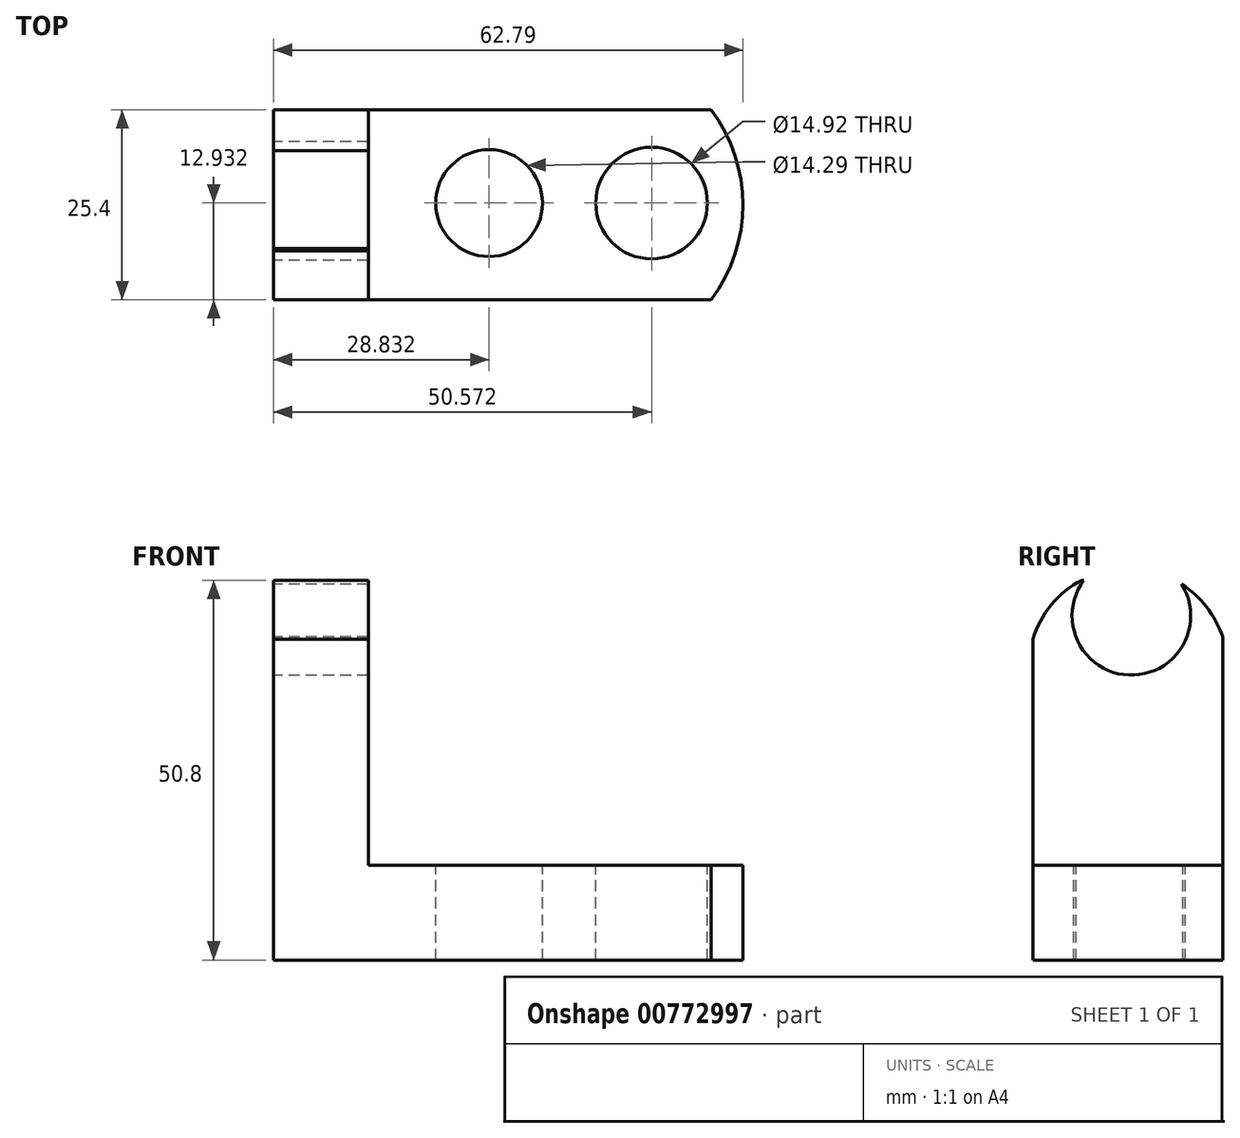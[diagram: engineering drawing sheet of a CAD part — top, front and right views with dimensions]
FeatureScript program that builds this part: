
annotation { "Feature Type Name" : "Feature", "Feature Type Description" : "" }
export const myFeature = defineFeature(function(context is Context, id is Id, definition is map)
    precondition{}
    {
        {
            var Q0;
            Q0=qCreatedBy(makeId("Front.planeOp"),FACE);
            var sketch = newSketch(context, id + "F0", { "sketchPlane" : qUnion([Q0])});
            skLineSegment(sketch, "E0", {"start": v(0, 0) * mm, "end": v(63.5, 0) * mm});
            skLineSegment(sketch, "E1", {"start": v(63.5, 0) * mm, "end": v(63.5, 50.8) * mm});
            skLineSegment(sketch, "E2", {"start": v(63.5, 50.8) * mm, "end": v(0, 50.8) * mm});
            skLineSegment(sketch, "E3", {"start": v(0, 50.8) * mm, "end": v(0, 0) * mm});
            skSolve(sketch);
        }
        {
            var Q0;
            Q0 = qSketchRegion(id + "F0", true);
            extrude(context, id + "F1", {"entities" : qUnion([Q0]), "depth" : 25.4 * mm, "offsetDistance" : 25.4 * mm});
        }
        {
            var Q0;
            Q0=makeQuery(id+"F1.opExtrude","CAP_FACE",FACE,{"disambiguationData":[OSD([sQuery(id+"F0.wireOp",EDGE,"E0"),sQuery(id+"F0.wireOp",EDGE,"E1"),sQuery(id+"F0.wireOp",EDGE,"E2"),sQuery(id+"F0.wireOp",EDGE,"E3")])],"isStart":false});
            var sketch = newSketch(context, id + "F2", { "sketchPlane" : qUnion([Q0])});
            skLineSegment(sketch, "E4", {"start": v(12.7, 50.8) * mm, "end": v(12.7, 12.7) * mm});
            skLineSegment(sketch, "E5", {"start": v(12.7, 12.7) * mm, "end": v(63.5, 12.7) * mm});
            skSolve(sketch);
        }
        {
            var Q0;
            Q0 = qSketchRegion(id + "F2", true);
            var Q1;
            {var subQ0=sQuery(id+"F2.wireOp",EDGE,"E4");Q1=makeQuery(id+"F2.imprint","IMPRINT",FACE,{"disambiguationData":[TD([[makeQuery(id+"F2.imprint","IMPRINT",EDGE,{"derivedFrom":subQ0}),1.0]])]});}
            extrude(context, id + "F3", {"entities" : qUnion([Q0, Q1]), "operationType" : NewBodyOperationType.REMOVE, "oppositeDirection" : true, "depth" : 25.4 * mm, "offsetDistance" : 25.4 * mm});
        }
        {
            var Q0;
            Q0=makeQuery(id+"F1.opExtrude","SWEPT_FACE",FACE,{"disambiguationData":[OSD([sQuery(id+"F0.wireOp",EDGE,"E3")])]});
            var sketch = newSketch(context, id + "F4", { "sketchPlane" : qUnion([Q0])});
            skArc(sketch, "E6", {"start": v(5.86, 50.8) * mm, "mid": v(12.2, 38.1) * mm, "end": v(18.56, 50.8) * mm});
            skSolve(sketch);
        }
        {
            var Q0;
            Q0 = qSketchRegion(id + "F4", true);
            var Q1;
            {var subQ0=sQuery(id+"F4.wireOp",EDGE,"E6");Q1=makeQuery(id+"F4.imprint","IMPRINT",FACE,{"disambiguationData":[TD([[makeQuery(id+"F4.imprint","IMPRINT",EDGE,{"derivedFrom":subQ0}),1.0]])]});}
            extrude(context, id + "F5", {"entities" : qUnion([Q0, Q1]), "operationType" : NewBodyOperationType.REMOVE, "oppositeDirection" : true, "depth" : 25.4 * mm, "offsetDistance" : 25.4 * mm});
        }
        {
            var Q0;
            Q0=makeQuery(id+"F1.opExtrude","SWEPT_FACE",FACE,{"disambiguationData":[OSD([sQuery(id+"F0.wireOp",EDGE,"E3")])]});
            var sketch = newSketch(context, id + "F6", { "sketchPlane" : qUnion([Q0])});
            skArc(sketch, "E7", {"start": v(25.4, 42.9) * mm, "mid": v(12.81, 52.33) * mm, "end": v(0, 43.22) * mm});
            skSolve(sketch);
        }
        {
            var Q0;
            Q0 = qSketchRegion(id + "F6", true);
            var Q1;
            {var subQ0=sQuery(id+"F6.wireOp",EDGE,"E7");var subQ1=sQuery(id+"F0.wireOp",EDGE,"E3");var subQ2=makeQuery(id+"F1.opExtrude","CAP_EDGE",EDGE,{"disambiguationData":[OSD([subQ1])],"isStart":true});var subQ3=makeQuery(id+"F6.imprint","INTERSECT",VERTEX,{"derivedFrom":[subQ2,subQ0]});Q1=makeQuery(id+"F6.imprint","IMPRINT",FACE,{"disambiguationData":[TD([[makeQuery(id+"F6.imprint","IMPRINT",EDGE,{"disambiguationData":[TD([[subQ3,1.0]])],"derivedFrom":subQ0}),-1.0]])]});}
            var Q2;
            {var subQ0=sQuery(id+"F6.wireOp",EDGE,"E7");var subQ1=sQuery(id+"F0.wireOp",EDGE,"E3");var subQ2=makeQuery(id+"F1.opExtrude","CAP_EDGE",EDGE,{"disambiguationData":[OSD([subQ1])],"isStart":false});var subQ3=makeQuery(id+"F6.imprint","INTERSECT",VERTEX,{"derivedFrom":[subQ2,subQ0]});Q2=makeQuery(id+"F6.imprint","IMPRINT",FACE,{"disambiguationData":[TD([[makeQuery(id+"F6.imprint","IMPRINT",EDGE,{"disambiguationData":[TD([[subQ3,-1.0]])],"derivedFrom":subQ0}),-1.0]])]});}
            extrude(context, id + "F7", {"entities" : qUnion([Q0, Q1, Q2]), "operationType" : NewBodyOperationType.REMOVE, "oppositeDirection" : true, "depth" : 25.4 * mm, "offsetDistance" : 25.4 * mm});
        }
        {
            var Q0;
            Q0=makeQuery(id+"F3.boolean.opBoolean","COPY",FACE,{"derivedFrom":makeQuery(id+"F3.opExtrude","SWEPT_FACE",FACE,{"disambiguationData":[OSD([sQuery(id+"F2.wireOp",EDGE,"E5")])]})});
            var sketch = newSketch(context, id + "F8", { "sketchPlane" : qUnion([Q0])});
            skCircle(sketch, "E8", {"center": v(28.83, -12.47) * mm, "radius": 7.14 * mm});
            skCircle(sketch, "E9", {"center": v(50.57, -12.47) * mm, "radius": 7.46 * mm});
            skSolve(sketch);
        }
        {
            var Q0;
            Q0=makeQuery(id+"F8.imprint","IMPRINT",FACE,{"disambiguationData":[TD([[makeQuery(id+"F8.imprint","IMPRINT",EDGE,{"derivedFrom":sQuery(id+"F8.wireOp",EDGE,"E8")}),1.0]])]});
            var Q1;
            Q1=makeQuery(id+"F8.imprint","IMPRINT",FACE,{"disambiguationData":[TD([[makeQuery(id+"F8.imprint","IMPRINT",EDGE,{"derivedFrom":sQuery(id+"F8.wireOp",EDGE,"E9")}),1.0]])]});
            extrude(context, id + "F9", {"entities" : qUnion([Q0, Q1]), "operationType" : NewBodyOperationType.REMOVE, "oppositeDirection" : true, "depth" : 25.4 * mm, "offsetDistance" : 25.4 * mm});
        }
        {
            var Q0;
            Q0=makeQuery(id+"F3.boolean.opBoolean","COPY",FACE,{"derivedFrom":makeQuery(id+"F3.opExtrude","SWEPT_FACE",FACE,{"disambiguationData":[OSD([sQuery(id+"F2.wireOp",EDGE,"E5")])]})});
            var sketch = newSketch(context, id + "F10", { "sketchPlane" : qUnion([Q0])});
            skArc(sketch, "E10", {"start": v(54.92, -25.4) * mm, "mid": v(63.85, -12.7) * mm, "end": v(54.92, 0) * mm});
            skSolve(sketch);
        }
        {
            var Q0;
            Q0 = qSketchRegion(id + "F10", true);
            var Q1;
            {var subQ0=sQuery(id+"F10.wireOp",EDGE,"E10");var subQ1=sQuery(id+"F2.wireOp",EDGE,"E5");var subQ2=makeQuery(id+"F3.boolean.opBoolean","COPY",EDGE,{"derivedFrom":makeQuery(id+"F3.opExtrude","CAP_EDGE",EDGE,{"disambiguationData":[OSD([subQ1])],"isStart":true})});var subQ3=makeQuery(id+"F10.imprint","INTERSECT",VERTEX,{"derivedFrom":[subQ2,subQ0]});Q1=makeQuery(id+"F10.imprint","IMPRINT",FACE,{"disambiguationData":[TD([[makeQuery(id+"F10.imprint","IMPRINT",EDGE,{"disambiguationData":[TD([[subQ3,-1.0]])],"derivedFrom":subQ0}),-1.0]])]});}
            var Q2;
            {var subQ0=sQuery(id+"F10.wireOp",EDGE,"E10");var subQ1=sQuery(id+"F2.wireOp",EDGE,"E5");var subQ2=makeQuery(id+"F3.boolean.opBoolean","COPY",EDGE,{"derivedFrom":makeQuery(id+"F3.opExtrude","CAP_EDGE",EDGE,{"disambiguationData":[OSD([subQ1])],"isStart":false})});var subQ3=makeQuery(id+"F10.imprint","INTERSECT",VERTEX,{"derivedFrom":[subQ2,subQ0]});Q2=makeQuery(id+"F10.imprint","IMPRINT",FACE,{"disambiguationData":[TD([[makeQuery(id+"F10.imprint","IMPRINT",EDGE,{"disambiguationData":[TD([[subQ3,1.0]])],"derivedFrom":subQ0}),-1.0]])]});}
            extrude(context, id + "F11", {"entities" : qUnion([Q0, Q1, Q2]), "operationType" : NewBodyOperationType.ADD, "depth" : 25.4 * mm, "offsetDistance" : 25.4 * mm});
        }
        {
            var Q0;
            {var subQ0=sQuery(id+"F2.wireOp",EDGE,"E5");var subQ1=makeQuery(id+"F3.boolean.opBoolean","COPY",EDGE,{"derivedFrom":makeQuery(id+"F3.opExtrude","CAP_EDGE",EDGE,{"disambiguationData":[OSD([subQ0])],"isStart":false})});var subQ2=sQuery(id+"F0.wireOp",EDGE,"E1");var subQ3=makeQuery(id+"F3.boolean.opBoolean","COPY",EDGE,{"derivedFrom":makeQuery(id+"F3.opExtrude","SWEPT_EDGE",EDGE,{"disambiguationData":[OSD([subQ2,subQ0])]})});var subQ4=makeQuery(id+"F10.imprint","INTERSECT",VERTEX,{"derivedFrom":[subQ3,subQ1]});var subQ5=sQuery(id+"F10.wireOp",EDGE,"E10");var subQ6=makeQuery(id+"F10.imprint","INTERSECT",VERTEX,{"derivedFrom":[subQ1,subQ5]});Q0=makeQuery(id+"F11.opExtrude","CAP_FACE",FACE,{"disambiguationData":[OSD([subQ2,subQ0,subQ5]),TDD([makeQuery(id+"F10.imprint","IMPRINT",EDGE,{"disambiguationData":[TD([[subQ6,1.0]])],"derivedFrom":subQ5}),makeQuery(id+"F10.imprint","IMPRINT",EDGE,{"disambiguationData":[TD([[subQ4,-1.0]])],"derivedFrom":subQ3}),makeQuery(id+"F10.imprint","IMPRINT",EDGE,{"disambiguationData":[TD([[subQ6,-1.0]])],"derivedFrom":subQ1})])],"isStart":false});}
            var Q1;
            {var subQ0=sQuery(id+"F2.wireOp",EDGE,"E5");var subQ1=makeQuery(id+"F3.boolean.opBoolean","COPY",EDGE,{"derivedFrom":makeQuery(id+"F3.opExtrude","CAP_EDGE",EDGE,{"disambiguationData":[OSD([subQ0])],"isStart":true})});var subQ2=sQuery(id+"F0.wireOp",EDGE,"E1");var subQ3=makeQuery(id+"F3.boolean.opBoolean","COPY",EDGE,{"derivedFrom":makeQuery(id+"F3.opExtrude","SWEPT_EDGE",EDGE,{"disambiguationData":[OSD([subQ2,subQ0])]})});var subQ4=makeQuery(id+"F10.imprint","INTERSECT",VERTEX,{"derivedFrom":[subQ3,subQ1]});var subQ5=sQuery(id+"F10.wireOp",EDGE,"E10");var subQ6=makeQuery(id+"F10.imprint","INTERSECT",VERTEX,{"derivedFrom":[subQ1,subQ5]});Q1=makeQuery(id+"F11.opExtrude","CAP_FACE",FACE,{"disambiguationData":[OSD([subQ2,subQ0,subQ5]),TDD([makeQuery(id+"F10.imprint","IMPRINT",EDGE,{"disambiguationData":[TD([[subQ6,-1.0]])],"derivedFrom":subQ5}),makeQuery(id+"F10.imprint","IMPRINT",EDGE,{"disambiguationData":[TD([[subQ4,1.0]])],"derivedFrom":subQ3}),makeQuery(id+"F10.imprint","IMPRINT",EDGE,{"disambiguationData":[TD([[subQ6,-1.0]])],"derivedFrom":subQ1})])],"isStart":false});}
            extrude(context, id + "F12", {"entities" : qUnion([Q0, Q1]), "operationType" : NewBodyOperationType.REMOVE, "oppositeDirection" : true, "depth" : 25.4 * mm, "offsetDistance" : 25.4 * mm});
        }
        {
            var Q0;
            {var subQ0=sQuery(id+"F2.wireOp",EDGE,"E5");var subQ1=makeQuery(id+"F3.boolean.opBoolean","COPY",EDGE,{"derivedFrom":makeQuery(id+"F3.opExtrude","CAP_EDGE",EDGE,{"disambiguationData":[OSD([subQ0])],"isStart":false})});var subQ2=sQuery(id+"F0.wireOp",EDGE,"E1");var subQ3=makeQuery(id+"F3.boolean.opBoolean","COPY",EDGE,{"derivedFrom":makeQuery(id+"F3.opExtrude","SWEPT_EDGE",EDGE,{"disambiguationData":[OSD([subQ2,subQ0])]})});var subQ4=makeQuery(id+"F10.imprint","INTERSECT",VERTEX,{"derivedFrom":[subQ3,subQ1]});var subQ5=sQuery(id+"F10.wireOp",EDGE,"E10");var subQ6=makeQuery(id+"F10.imprint","INTERSECT",VERTEX,{"derivedFrom":[subQ1,subQ5]});var subQ8=makeQuery(id+"F3.boolean.opBoolean","COPY",EDGE,{"derivedFrom":makeQuery(id+"F3.opExtrude","CAP_EDGE",EDGE,{"disambiguationData":[OSD([subQ0])],"isStart":true})});var subQ9=makeQuery(id+"F10.imprint","INTERSECT",VERTEX,{"derivedFrom":[subQ3,subQ8]});var subQ10=makeQuery(id+"F10.imprint","INTERSECT",VERTEX,{"derivedFrom":[subQ8,subQ5]});Q0=makeQuery(id+"F12.boolean.opBoolean","MERGE",FACE,{"derivedFrom":[makeQuery(id+"F3.boolean.opBoolean","COPY",FACE,{"derivedFrom":makeQuery(id+"F3.opExtrude","SWEPT_FACE",FACE,{"disambiguationData":[OSD([subQ0])]})}),makeQuery(id+"F12.opExtrude","CAP_FACE",FACE,{"disambiguationData":[OSD([subQ2,subQ0,subQ5]),TDD([makeQuery(id+"F11.opExtrude","CAP_FACE",FACE,{"disambiguationData":[OSD([subQ2,subQ0,subQ5]),TDD([makeQuery(id+"F10.imprint","IMPRINT",EDGE,{"disambiguationData":[TD([[subQ10,-1.0]])],"derivedFrom":subQ5}),makeQuery(id+"F10.imprint","IMPRINT",EDGE,{"disambiguationData":[TD([[subQ9,1.0]])],"derivedFrom":subQ3}),makeQuery(id+"F10.imprint","IMPRINT",EDGE,{"disambiguationData":[TD([[subQ10,-1.0]])],"derivedFrom":subQ8})])],"isStart":false})])],"isStart":false}),makeQuery(id+"F12.opExtrude","CAP_FACE",FACE,{"disambiguationData":[OSD([subQ2,subQ0,subQ5]),TDD([makeQuery(id+"F11.opExtrude","CAP_FACE",FACE,{"disambiguationData":[OSD([subQ2,subQ0,subQ5]),TDD([makeQuery(id+"F10.imprint","IMPRINT",EDGE,{"disambiguationData":[TD([[subQ6,1.0]])],"derivedFrom":subQ5}),makeQuery(id+"F10.imprint","IMPRINT",EDGE,{"disambiguationData":[TD([[subQ4,-1.0]])],"derivedFrom":subQ3}),makeQuery(id+"F10.imprint","IMPRINT",EDGE,{"disambiguationData":[TD([[subQ6,-1.0]])],"derivedFrom":subQ1})])],"isStart":false})])],"isStart":false})]});}
            var sketch = newSketch(context, id + "F13", { "sketchPlane" : qUnion([Q0])});
            skArc(sketch, "E11", {"start": v(58.54, -25.4) * mm, "mid": v(62.79, -12.7) * mm, "end": v(58.54, 0) * mm});
            skSolve(sketch);
        }
        {
            var Q0;
            {var subQ0=sQuery(id+"F13.wireOp",EDGE,"E11");Q0=makeQuery(id+"F13.imprint","IMPRINT",FACE,{"disambiguationData":[TD([[makeQuery(id+"F13.imprint","IMPRINT",EDGE,{"derivedFrom":subQ0}),-1.0]])]});}
            extrude(context, id + "F14", {"entities" : qUnion([Q0]), "operationType" : NewBodyOperationType.REMOVE, "oppositeDirection" : true, "depth" : 25.4 * mm, "offsetDistance" : 25.4 * mm});
        }
    });
